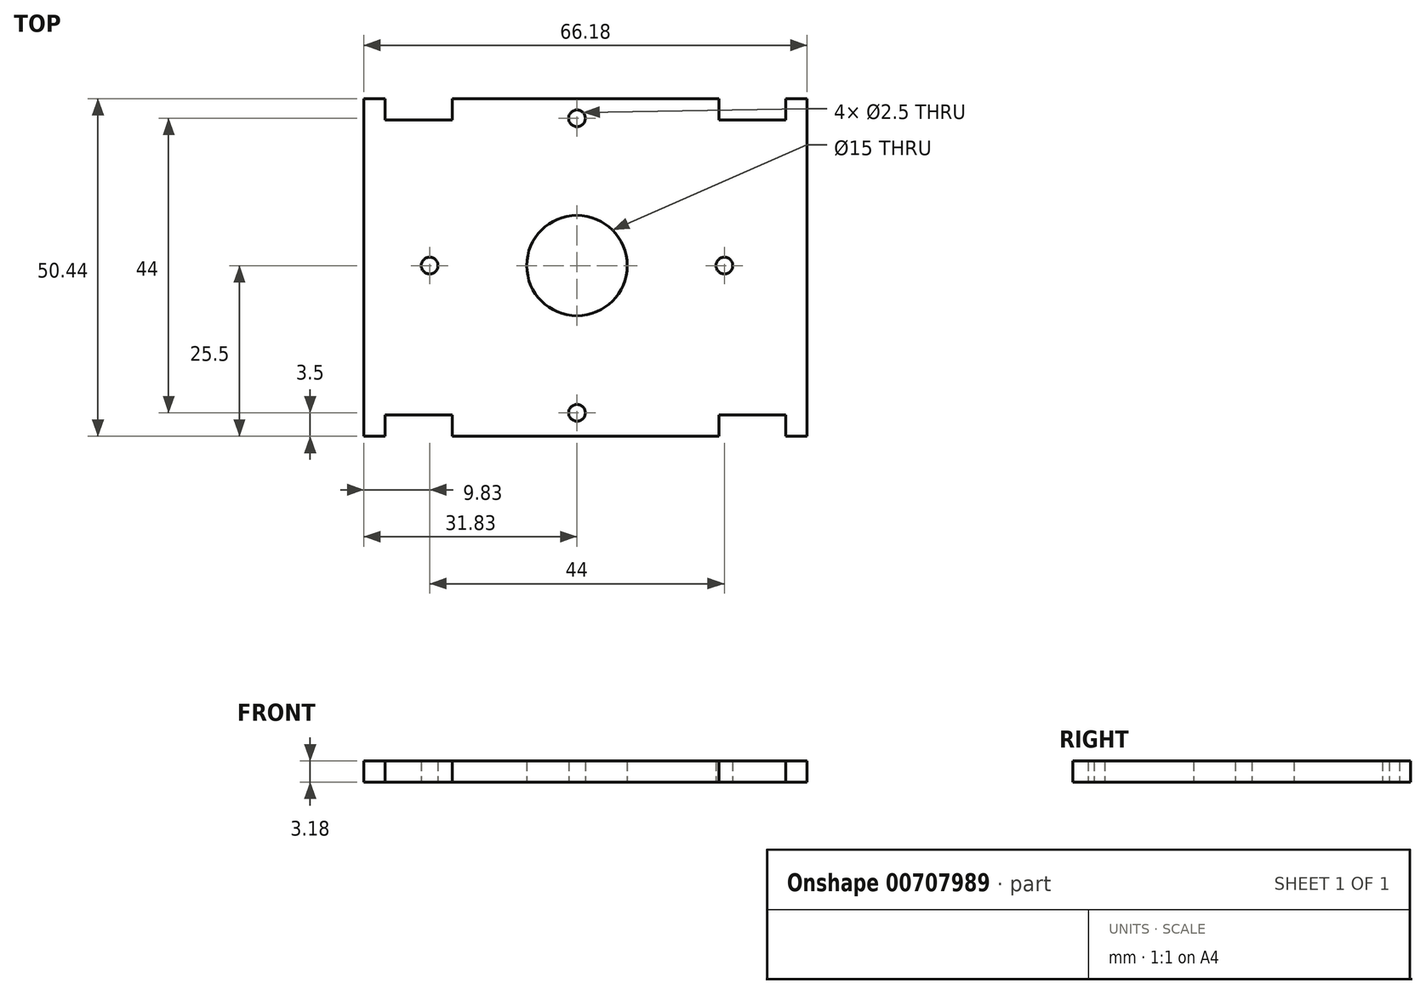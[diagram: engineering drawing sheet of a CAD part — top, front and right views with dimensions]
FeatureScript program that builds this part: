
annotation { "Feature Type Name" : "Feature", "Feature Type Description" : "" }
export const myFeature = defineFeature(function(context is Context, id is Id, definition is map)
    precondition{}
    {
        {
            var Q0;
            Q0=qCreatedBy(makeId("Top.planeOp"), FACE);
            var sketch = newSketch(context, id + "F0", { "sketchPlane" : qUnion([Q0])});
            skLineSegment(sketch, "E0.0.1", {"start": v(-31.83, 24.94) * mm, "end": v(-31.83, -25.5) * mm});
            skLineSegment(sketch, "E0.0.2", {"start": v(-31.83, -25.5) * mm, "end": v(-28.65, -25.5) * mm});
            skLineSegment(sketch, "E0.0.3", {"start": v(34.35, -25.5) * mm, "end": v(34.35, 24.94) * mm});
            skPoint(sketch, "E1.middle", {"position": v(0, 0) * mm});
            skLineSegment(sketch, "E2", {"start": v(0, 0) * mm, "end": v(22, 0) * mm, "construction": true});
            skLineSegment(sketch, "E3", {"start": v(0, 0) * mm, "end": v(0, 22) * mm, "construction": true});
            skCircle(sketch, "E4", {"center": v(0, 22) * mm, "radius": 1.25 * mm});
            skCircle(sketch, "E5", {"center": v(22, 0) * mm, "radius": 1.25 * mm});
            skCircle(sketch, "E6.MirrorC", {"center": v(0, -22) * mm, "radius": 1.25 * mm});
            skCircle(sketch, "E7.MirrorC", {"center": v(-22, 0) * mm, "radius": 1.25 * mm});
            skCircle(sketch, "E8", {"center": v(0, 0) * mm, "radius": 7.5 * mm});
            skLineSegment(sketch, "E9", {"start": v(-28.65, 24.94) * mm, "end": v(-28.65, 21.76) * mm});
            skLineSegment(sketch, "E10", {"start": v(-18.65, 21.76) * mm, "end": v(-18.65, 24.94) * mm});
            skLineSegment(sketch, "E11.trimOffspring", {"start": v(-28.65, 24.94) * mm, "end": v(-31.83, 24.94) * mm});
            skPoint(sketch, "E12.end.orphan", {"position": v(-18.65, 23.35) * mm});
            skPoint(sketch, "E12.start.orphan", {"position": v(-28.65, 23.35) * mm});
            skLineSegment(sketch, "E13.MirrorCS", {"start": v(21.17, 21.76) * mm, "end": v(21.17, 24.94) * mm});
            skLineSegment(sketch, "E14.MirrorCS", {"start": v(31.17, 24.94) * mm, "end": v(31.17, 21.76) * mm});
            skPoint(sketch, "E15.orphan", {"position": v(-31.17, 21.76) * mm});
            skLineSegment(sketch, "E16.trimOffspring", {"start": v(21.17, 21.76) * mm, "end": v(31.17, 21.76) * mm});
            skPoint(sketch, "E17.orphan", {"position": v(31.17, 21.76) * mm});
            skLineSegment(sketch, "E18.trimOffspring", {"start": v(-18.65, 21.76) * mm, "end": v(-28.65, 21.76) * mm});
            skLineSegment(sketch, "E19.MirrorCS", {"start": v(31.17, -25.5) * mm, "end": v(31.17, -22.32) * mm});
            skLineSegment(sketch, "E20.MirrorCS", {"start": v(21.17, -22.32) * mm, "end": v(31.17, -22.32) * mm});
            skLineSegment(sketch, "E21.MirrorCS", {"start": v(21.17, -22.32) * mm, "end": v(21.17, -25.5) * mm});
            skLineSegment(sketch, "E22.MirrorCS", {"start": v(-18.65, -22.32) * mm, "end": v(-18.65, -25.5) * mm});
            skLineSegment(sketch, "E23.MirrorCS", {"start": v(-18.65, -22.32) * mm, "end": v(-28.65, -22.32) * mm});
            skLineSegment(sketch, "E24.MirrorCS", {"start": v(-28.65, -25.5) * mm, "end": v(-28.65, -22.32) * mm});
            skLineSegment(sketch, "E25", {"start": v(34.35, 24.94) * mm, "end": v(31.17, 24.94) * mm});
            skLineSegment(sketch, "E26", {"start": v(31.17, -25.5) * mm, "end": v(34.35, -25.5) * mm});
            skLineSegment(sketch, "E27", {"start": v(-18.65, 24.94) * mm, "end": v(21.17, 24.94) * mm});
            skLineSegment(sketch, "E28", {"start": v(-18.65, -25.5) * mm, "end": v(21.17, -25.5) * mm});
            skSolve(sketch);
        }
        {
            var Q0;
            Q0 = qSketchRegion(id + "F0", true);
            extrude(context, id + "F1", {"entities" : qUnion([Q0]), "depth" : 3.17 * mm, "offsetDistance" : 25 * mm});
        }
    });
